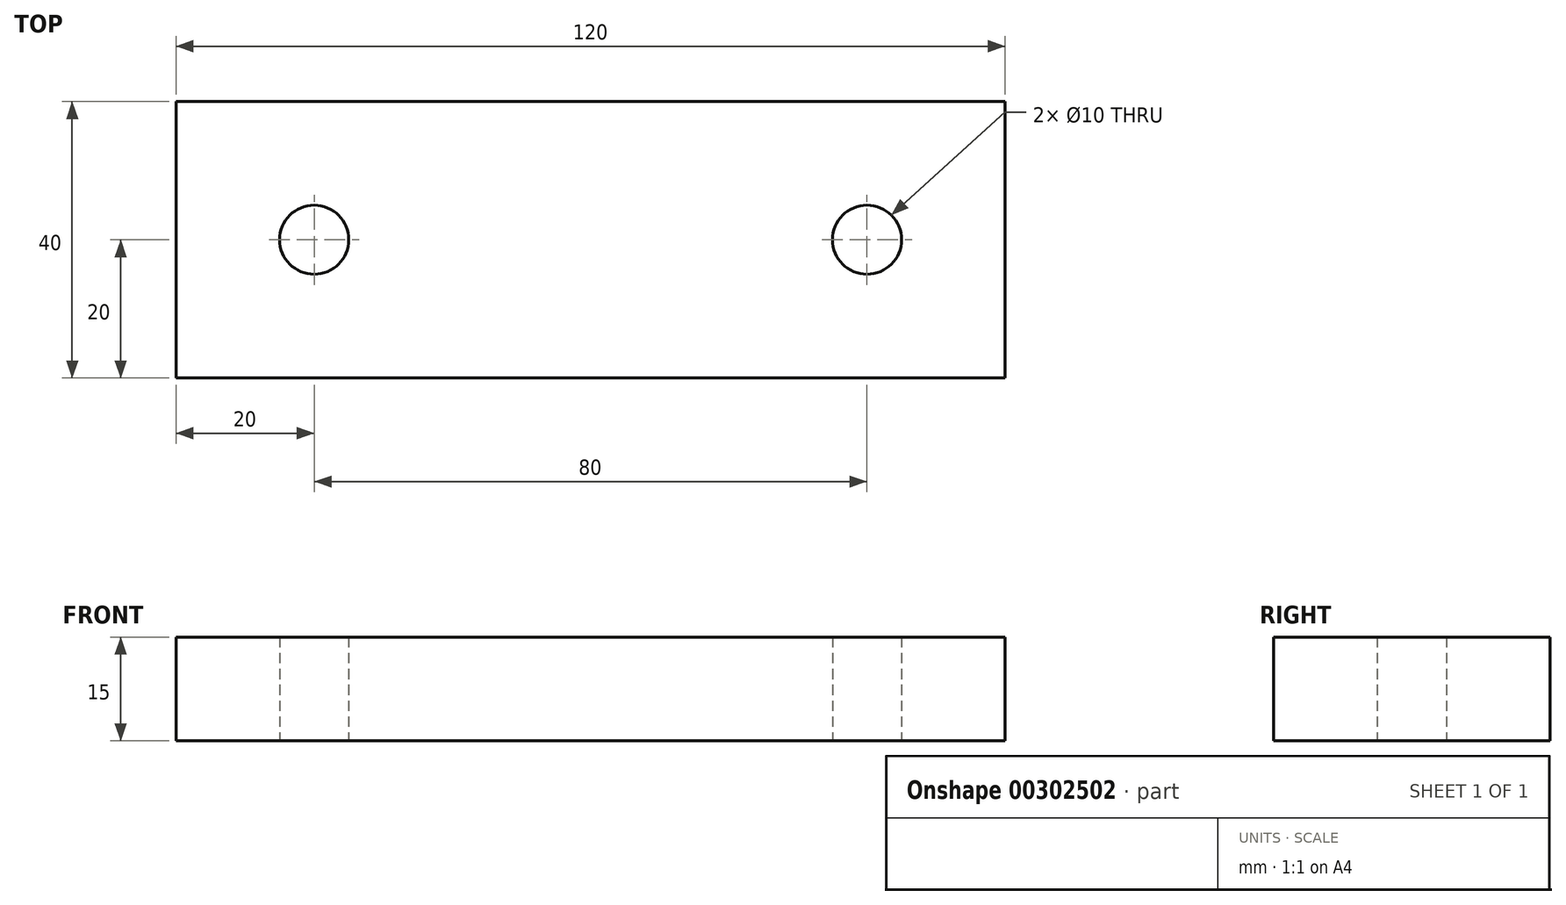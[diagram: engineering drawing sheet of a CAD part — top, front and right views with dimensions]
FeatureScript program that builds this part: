
annotation { "Feature Type Name" : "Feature", "Feature Type Description" : "" }
export const myFeature = defineFeature(function(context is Context, id is Id, definition is map)
    precondition{}
    {
        {
            var Q0;
            Q0=qCreatedBy(makeId("Top.planeOp"),FACE);
            var sketch = newSketch(context, id + "F0", { "sketchPlane" : qUnion([Q0])});
            skLineSegment(sketch, "E0.bottom", {"start": v(0, 0) * mm, "end": v(120, 0) * mm});
            skLineSegment(sketch, "E0.top", {"start": v(0, 40) * mm, "end": v(120, 40) * mm});
            skLineSegment(sketch, "E0.left", {"start": v(0, 0) * mm, "end": v(0, 40) * mm});
            skLineSegment(sketch, "E0.right", {"start": v(120, 0) * mm, "end": v(120, 40) * mm});
            skCircle(sketch, "E1", {"center": v(20, 20) * mm, "radius": 5 * mm});
            skLineSegment(sketch, "E2", {"start": v(60, 0) * mm, "end": v(60, 23.5) * mm, "construction": true});
            skCircle(sketch, "E3.MirrorC", {"center": v(100, 20) * mm, "radius": 5 * mm});
            skSolve(sketch);
        }
        {
            var Q0;
            Q0 = qSketchRegion(id + "F0", true);
            extrude(context, id + "F1", {"entities" : qUnion([Q0]), "depth" : 15 * mm});
        }
    });
